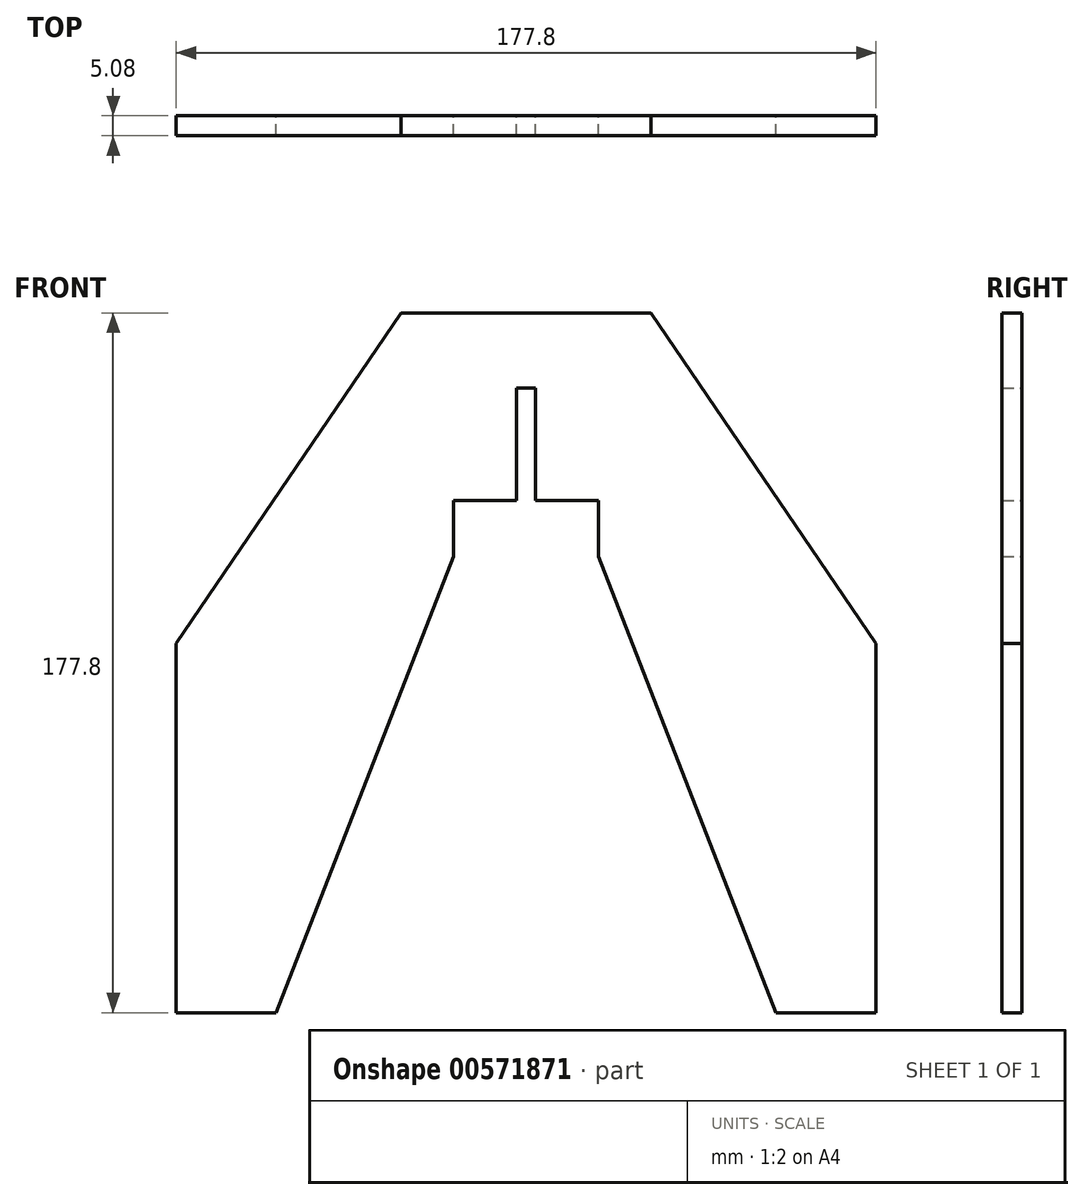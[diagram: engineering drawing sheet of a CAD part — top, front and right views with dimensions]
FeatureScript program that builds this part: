
annotation { "Feature Type Name" : "Feature", "Feature Type Description" : "" }
export const myFeature = defineFeature(function(context is Context, id is Id, definition is map)
    precondition{}
    {
        {
            var Q0;
            Q0=qCreatedBy(makeId("Front.planeOp"),FACE);
            var sketch = newSketch(context, id + "F0", { "sketchPlane" : qUnion([Q0])});
            skLineSegment(sketch, "E0", {"start": v(-31.75, 0) * mm, "end": v(31.75, 0) * mm});
            skLineSegment(sketch, "E1", {"start": v(31.75, 0) * mm, "end": v(88.9, -84) * mm});
            skLineSegment(sketch, "E2", {"start": v(88.9, -84) * mm, "end": v(88.9, -177.8) * mm});
            skLineSegment(sketch, "E3", {"start": v(88.9, -177.8) * mm, "end": v(63.5, -177.8) * mm});
            skLineSegment(sketch, "E4", {"start": v(2.39, -19.05) * mm, "end": v(-2.39, -19.05) * mm});
            skLineSegment(sketch, "E5", {"start": v(-63.5, -177.8) * mm, "end": v(-88.9, -177.8) * mm});
            skLineSegment(sketch, "E6", {"start": v(-88.9, -177.8) * mm, "end": v(-88.9, -84) * mm});
            skLineSegment(sketch, "E7", {"start": v(-88.9, -84) * mm, "end": v(-31.75, 0) * mm});
            skLineSegment(sketch, "E8", {"start": v(-2.39, -19.05) * mm, "end": v(-2.39, -47.62) * mm});
            skLineSegment(sketch, "E9", {"start": v(2.39, -19.05) * mm, "end": v(2.39, -47.62) * mm});
            skLineSegment(sketch, "E10", {"start": v(-2.39, -47.62) * mm, "end": v(-18.39, -47.62) * mm});
            skLineSegment(sketch, "E11", {"start": v(2.39, -47.62) * mm, "end": v(18.39, -47.62) * mm});
            skLineSegment(sketch, "E12", {"start": v(-18.39, -47.62) * mm, "end": v(-18.39, -61.91) * mm});
            skLineSegment(sketch, "E13", {"start": v(-18.39, -61.91) * mm, "end": v(-63.5, -177.8) * mm});
            skLineSegment(sketch, "E14", {"start": v(18.39, -47.62) * mm, "end": v(18.39, -61.91) * mm});
            skLineSegment(sketch, "E15", {"start": v(18.39, -61.91) * mm, "end": v(63.5, -177.8) * mm});
            skSolve(sketch);
        }
        {
            var Q0;
            Q0=makeQuery(id+"F0.imprint","IMPRINT",FACE,{"disambiguationData":[TD([[makeQuery(id+"F0.imprint","IMPRINT",EDGE,{"derivedFrom":sQuery(id+"F0.wireOp",EDGE,"E0")}),-1.0]])]});
            extrude(context, id + "F1", {"entities" : qUnion([Q0]), "depth" : 5.08 * mm, "offsetDistance" : 25.4 * mm});
        }
    });
